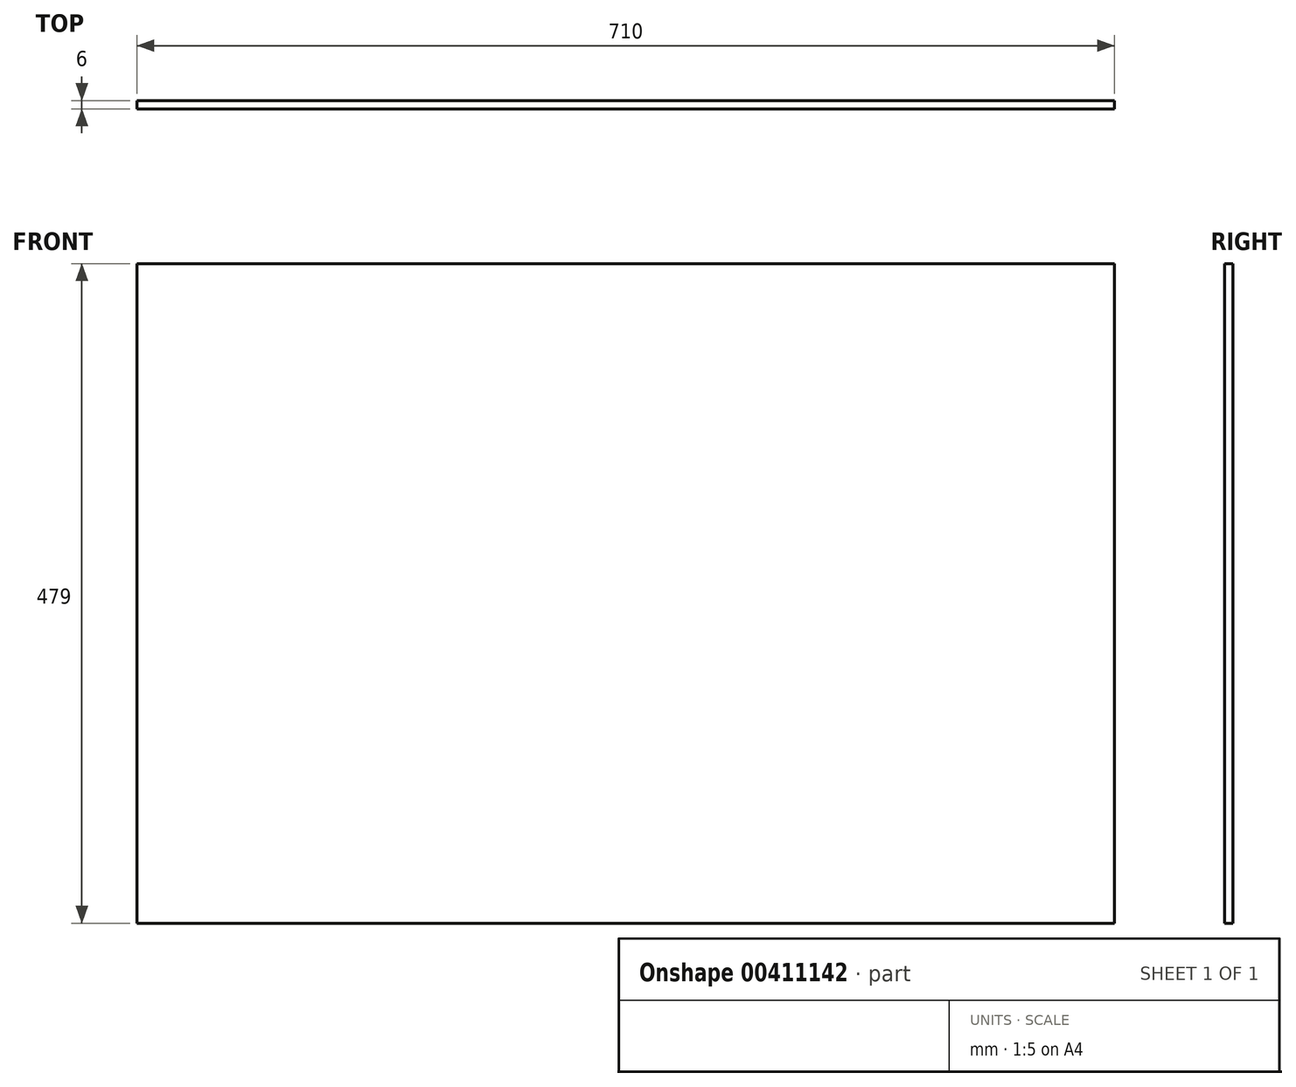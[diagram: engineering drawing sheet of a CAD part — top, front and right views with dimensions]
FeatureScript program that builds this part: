
annotation { "Feature Type Name" : "Feature", "Feature Type Description" : "" }
export const myFeature = defineFeature(function(context is Context, id is Id, definition is map)
    precondition{}
    {
        {
            var Q0;
            Q0=qCreatedBy(makeId("Front.planeOp"),FACE);
            var sketch = newSketch(context, id + "F0", { "sketchPlane" : qUnion([Q0])});
            skLineSegment(sketch, "E0.bottom", {"start": v(0, 0) * mm, "end": v(710, 0) * mm});
            skLineSegment(sketch, "E0.top", {"start": v(0, 479) * mm, "end": v(710, 479) * mm});
            skLineSegment(sketch, "E0.left", {"start": v(0, 0) * mm, "end": v(0, 479) * mm});
            skLineSegment(sketch, "E0.right", {"start": v(710, 0) * mm, "end": v(710, 479) * mm});
            skSolve(sketch);
        }
        {
            var Q0;
            Q0 = qSketchRegion(id + "F0", true);
            extrude(context, id + "F1", {"entities" : qUnion([Q0]), "depth" : 6 * mm});
        }
    });
